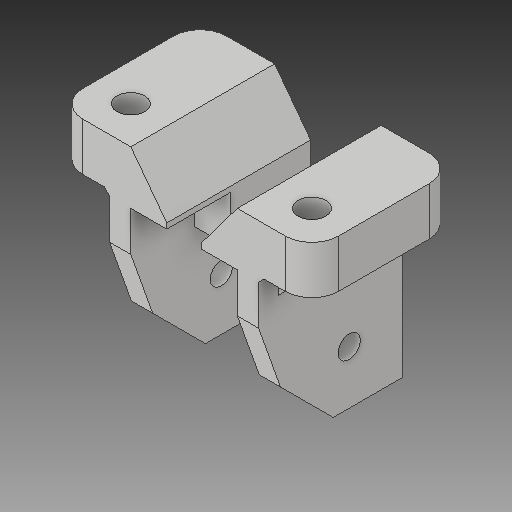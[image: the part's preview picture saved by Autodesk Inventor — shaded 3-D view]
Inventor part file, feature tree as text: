
AUTODESK INVENTOR PART (.ipt)
format: ipt  version: 2018 (Build 220112000, 112)  size: 201,216 bytes
history: native  units: mm
features: sketch x9, other x3
ambient origin geometry x8: Origin, YZ Plane, XZ Plane, XY Plane, X Axis, Y Axis, Z Axis, Center Point
bodies: Solid1 (feature_tree)
feature tree (12):
  other  "holder-GT2-x-carriage-left.ipt"
  other  "Solid1::holder-GT2-x-carriage-left.ipt"
  other  "TaggingFeature1"
  sketch  "Sketch1"  dims[d0=10.0mm]
  sketch  "Sketch2"
  sketch  "Sketch3"
  sketch  "Sketch4"
  sketch  "Sketch8"
  sketch  "Sketch9"
  sketch  "Sketch6"
  sketch  "Sketch11"
  sketch  "Sketch12"
